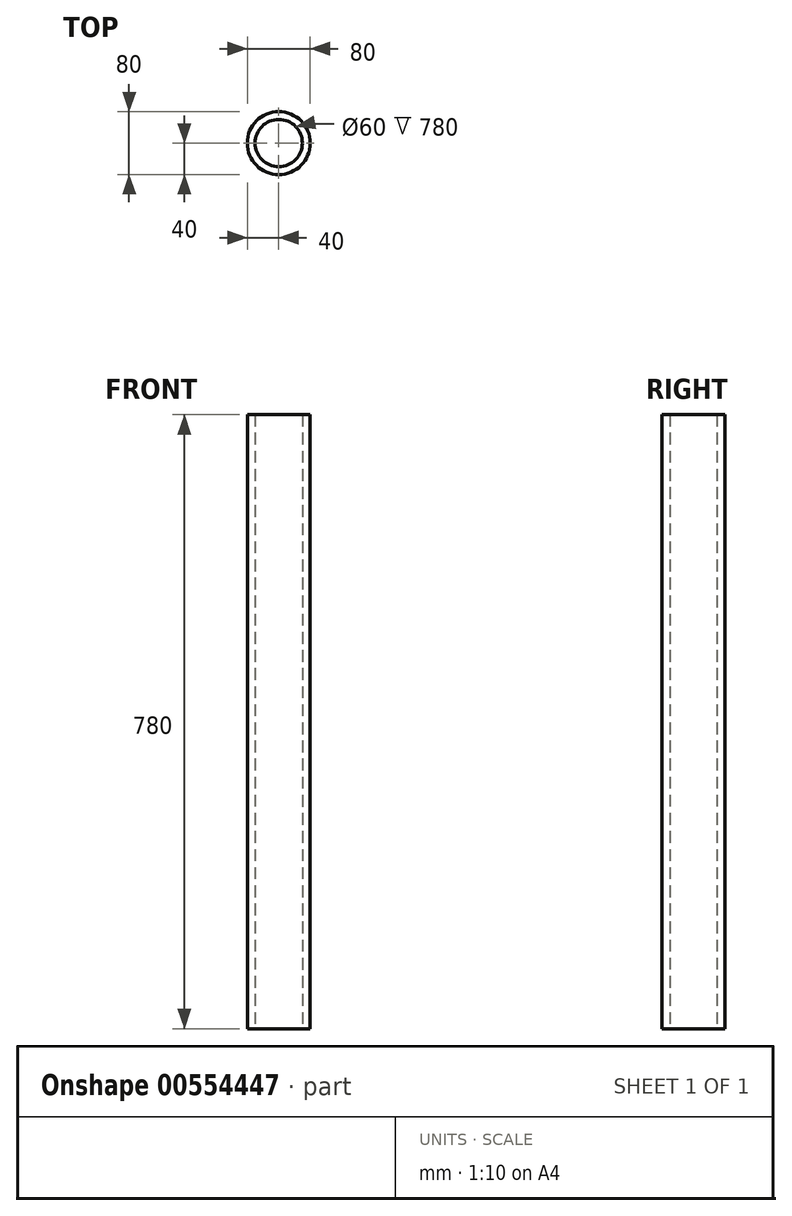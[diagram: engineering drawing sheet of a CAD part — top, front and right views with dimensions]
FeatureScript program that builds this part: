
annotation { "Feature Type Name" : "Feature", "Feature Type Description" : "" }
export const myFeature = defineFeature(function(context is Context, id is Id, definition is map)
    precondition{}
    {
        {
            var Q0;
            Q0=qCreatedBy(makeId("Top.planeOp"),FACE);
            var sketch = newSketch(context, id + "F0", { "sketchPlane" : qUnion([Q0])});
            skCircle(sketch, "E0", {"center": v(0, 0) * mm, "radius": 40 * mm});
            skCircle(sketch, "E1", {"center": v(0, 0) * mm, "radius": 30 * mm});
            skSolve(sketch);
        }
        {
            var Q0;
            Q0=makeQuery(id+"F0.imprint","IMPRINT",FACE,{"disambiguationData":[TD([[makeQuery(id+"F0.imprint","IMPRINT",EDGE,{"derivedFrom":sQuery(id+"F0.wireOp",EDGE,"E0")}),1.0]])]});
            extrude(context, id + "F1", {"entities" : qUnion([Q0]), "depth" : 780 * mm, "offsetDistance" : 25 * mm});
        }
    });
